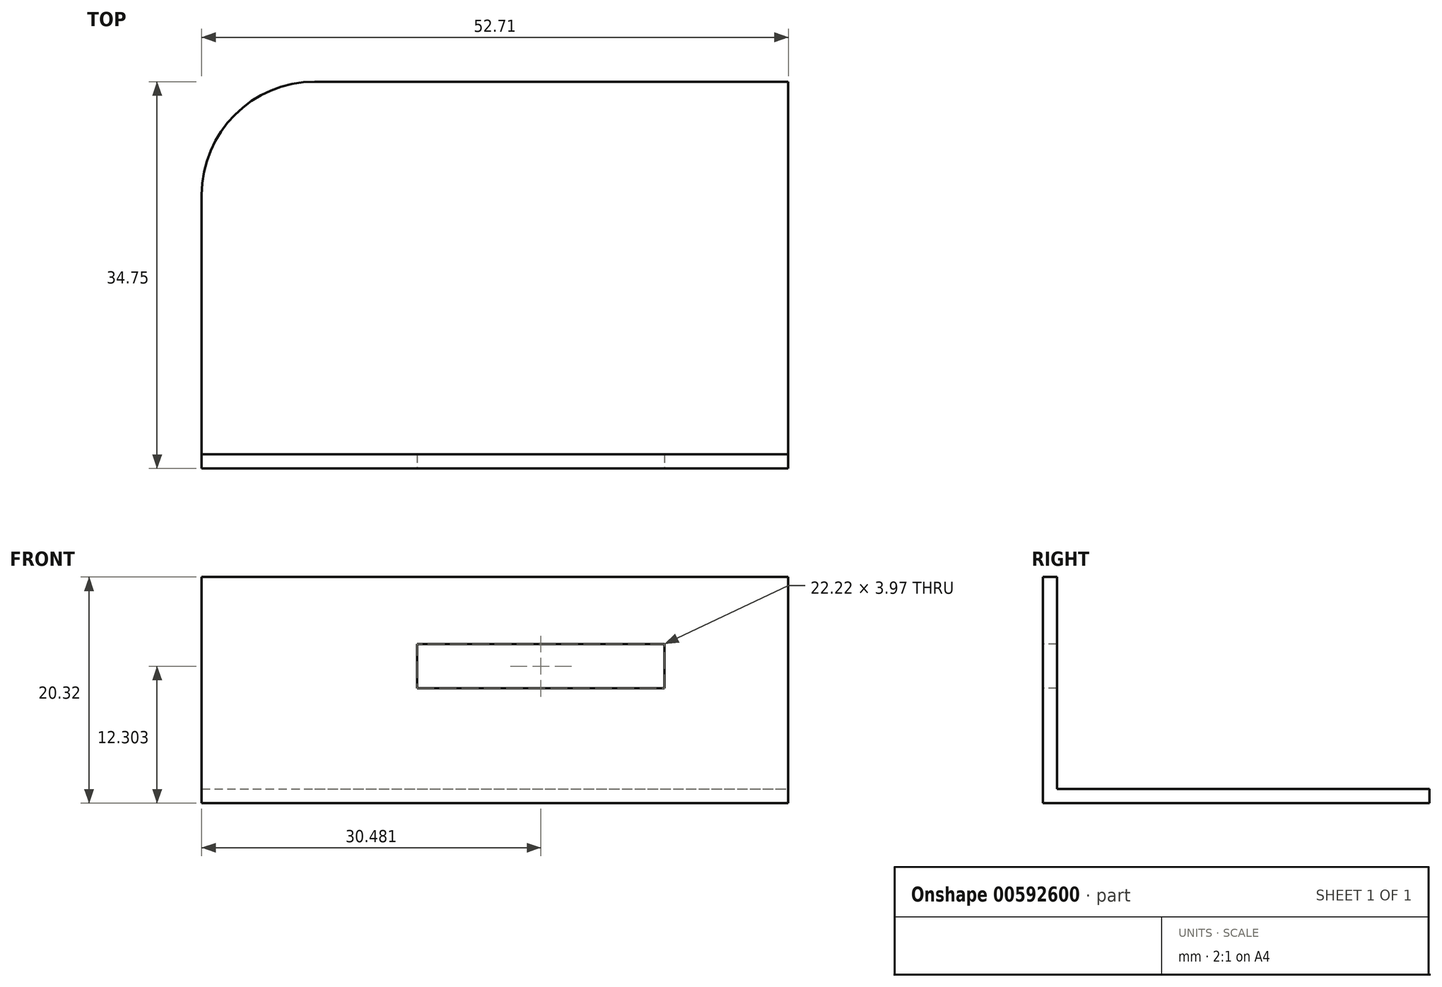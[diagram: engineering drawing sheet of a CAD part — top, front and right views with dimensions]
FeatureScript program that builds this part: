
annotation { "Feature Type Name" : "Feature", "Feature Type Description" : "" }
export const myFeature = defineFeature(function(context is Context, id is Id, definition is map)
    precondition{}
    {
        {
            var Q0;
            Q0=qCreatedBy(makeId("Top.planeOp"),FACE);
            var sketch = newSketch(context, id + "F0", { "sketchPlane" : qUnion([Q0])});
            skLineSegment(sketch, "E0.bottom", {"start": v(-64.95, 19.95) * mm, "end": v(-12.24, 19.95) * mm});
            skLineSegment(sketch, "E0.top", {"start": v(-64.95, -14.8) * mm, "end": v(-12.24, -14.8) * mm});
            skLineSegment(sketch, "E0.left", {"start": v(-64.95, 19.95) * mm, "end": v(-64.95, -14.8) * mm});
            skLineSegment(sketch, "E0.right", {"start": v(-12.24, 19.95) * mm, "end": v(-12.24, -14.8) * mm});
            skLineSegment(sketch, "E1.bottom", {"start": v(-63.68, 18.68) * mm, "end": v(-13.51, 18.68) * mm});
            skLineSegment(sketch, "E1.top", {"start": v(-63.68, -13.53) * mm, "end": v(-13.51, -13.53) * mm});
            skLineSegment(sketch, "E1.left", {"start": v(-63.68, 18.68) * mm, "end": v(-63.68, -13.53) * mm});
            skLineSegment(sketch, "E1.right", {"start": v(-13.51, 18.68) * mm, "end": v(-13.51, -13.53) * mm});
            skSolve(sketch);
        }
        {
            var Q0;
            Q0=makeQuery(id+"F0.imprint","IMPRINT",FACE,{"disambiguationData":[TD([[makeQuery(id+"F0.imprint","IMPRINT",EDGE,{"derivedFrom":sQuery(id+"F0.wireOp",EDGE,"E0.bottom")}),-1.0]])]});
            extrude(context, id + "F1", {"entities" : qUnion([Q0]), "depth" : 20.32 * mm, "offsetDistance" : 25.4 * mm});
        }
        {
            var Q0;
            Q0=makeQuery(id+"F0.imprint","IMPRINT",FACE,{"disambiguationData":[TD([[makeQuery(id+"F0.imprint","IMPRINT",EDGE,{"derivedFrom":sQuery(id+"F0.wireOp",EDGE,"E1.bottom")}),-1.0]])]});
            extrude(context, id + "F2", {"entities" : qUnion([Q0]), "operationType" : NewBodyOperationType.ADD, "depth" : 1.27 * mm, "offsetDistance" : 25.4 * mm});
        }
        {
            var Q0;
            Q0=makeQuery(id+"F1.opExtrude","SWEPT_EDGE",EDGE,{"disambiguationData":[OSD([sQuery(id+"F0.wireOp",EDGE,"E0.bottom"),sQuery(id+"F0.wireOp",EDGE,"E0.left")])]});
            var Q1;
            Q1=makeQuery(id+"F1.opExtrude","SWEPT_EDGE",EDGE,{"disambiguationData":[OSD([sQuery(id+"F0.wireOp",EDGE,"E1.bottom"),sQuery(id+"F0.wireOp",EDGE,"E1.left")])]});
            fillet(context, id + "F3", {"entities" : qUnion([Q0, Q1]), "radius" : 10.16 * mm, "tangentPropagation" : true, "allowEdgeOverflow" : false});
        }
        {
            var Q0;
            Q0=makeQuery(id+"F0.imprint","IMPRINT",FACE,{"disambiguationData":[TD([[makeQuery(id+"F0.imprint","IMPRINT",EDGE,{"derivedFrom":sQuery(id+"F0.wireOp",EDGE,"E0.bottom")}),-1.0]])]});
            var sketch = newSketch(context, id + "F4", { "sketchPlane" : qUnion([Q0])});
            skSolve(sketch);
        }
        {
            var Q0;
            Q0=makeQuery(id+"F1.opExtrude","SWEPT_FACE",FACE,{"disambiguationData":[OSD([sQuery(id+"F0.wireOp",EDGE,"E0.top")])]});
            var sketch = newSketch(context, id + "F5", { "sketchPlane" : qUnion([Q0])});
            skLineSegment(sketch, "E2.bottom", {"start": v(-64.95, 20.32) * mm, "end": v(-12.24, 20.32) * mm});
            skLineSegment(sketch, "E2.top", {"start": v(-64.95, 0) * mm, "end": v(-12.24, 0) * mm});
            skLineSegment(sketch, "E2.left", {"start": v(-64.95, 20.32) * mm, "end": v(-64.95, 0) * mm});
            skLineSegment(sketch, "E2.right", {"start": v(-12.24, 20.32) * mm, "end": v(-12.24, 0) * mm});
            skSolve(sketch);
        }
        {
            var Q0;
            Q0=makeQuery(id+"F1.opExtrude","SWEPT_FACE",FACE,{"disambiguationData":[OSD([sQuery(id+"F0.wireOp",EDGE,"E1.right")])]});
            var sketch = newSketch(context, id + "F6", { "sketchPlane" : qUnion([Q0])});
            skLineSegment(sketch, "E3.bottom", {"start": v(13.53, 10.8) * mm, "end": v(-8.52, 10.8) * mm});
            skLineSegment(sketch, "E3.top", {"start": v(13.53, 9.2) * mm, "end": v(-8.52, 9.2) * mm});
            skLineSegment(sketch, "E3.left", {"start": v(13.53, 10.8) * mm, "end": v(13.53, 9.2) * mm});
            skLineSegment(sketch, "E3.right", {"start": v(-8.52, 10.8) * mm, "end": v(-8.52, 9.2) * mm});
            skLineSegment(sketch, "E4.top", {"start": v(13.53, 7.94) * mm, "end": v(-8.52, 7.94) * mm});
            skLineSegment(sketch, "E4.left", {"start": v(13.53, 9.2) * mm, "end": v(13.53, 7.94) * mm});
            skLineSegment(sketch, "E4.right", {"start": v(-8.52, 9.2) * mm, "end": v(-8.52, 7.94) * mm});
            skSolve(sketch);
        }
        {
            var Q0;
            Q0=makeQuery(id+"F6.imprint","IMPRINT",FACE,{"disambiguationData":[TD([[makeQuery(id+"F6.imprint","IMPRINT",EDGE,{"derivedFrom":sQuery(id+"F6.wireOp",EDGE,"E3.top")}),1.0]])]});
            extrude(context, id + "F7", {"entities" : qUnion([Q0]), "operationType" : NewBodyOperationType.ADD, "depth" : 0.38 * mm, "offsetDistance" : 25.4 * mm});
        }
        {
            var Q0;
            Q0=makeQuery(id+"F1.opExtrude","SWEPT_FACE",FACE,{"disambiguationData":[OSD([sQuery(id+"F0.wireOp",EDGE,"E0.right")])]});
            var sketch = newSketch(context, id + "F8", { "sketchPlane" : qUnion([Q0])});
            skLineSegment(sketch, "E5.bottom", {"start": v(-13.53, 20.32) * mm, "end": v(19.95, 20.32) * mm});
            skLineSegment(sketch, "E5.top", {"start": v(-13.53, 1.27) * mm, "end": v(19.95, 1.27) * mm});
            skLineSegment(sketch, "E5.left", {"start": v(-13.53, 20.32) * mm, "end": v(-13.53, 1.27) * mm});
            skLineSegment(sketch, "E5.right", {"start": v(19.95, 20.32) * mm, "end": v(19.95, 1.27) * mm});
            skSolve(sketch);
        }
        {
            var Q0;
            Q0 = qSketchRegion(id + "F8", true);
            extrude(context, id + "F9", {"entities" : qUnion([Q0]), "operationType" : NewBodyOperationType.REMOVE, "oppositeDirection" : true, "depth" : 78.74 * mm, "offsetDistance" : 25.4 * mm});
        }
        {
            var Q0;
            Q0=makeQuery(id+"F5.imprint","IMPRINT",FACE,{"disambiguationData":[TD([[makeQuery(id+"F5.imprint","IMPRINT",EDGE,{"derivedFrom":sQuery(id+"F5.wireOp",EDGE,"E2.bottom")}),-1.0]])]});
            var sketch = newSketch(context, id + "F10", { "sketchPlane" : qUnion([Q0])});
            skLineSegment(sketch, "E6.bottom", {"start": v(-45.58, 14.29) * mm, "end": v(-23.36, 14.29) * mm});
            skLineSegment(sketch, "E6.top", {"start": v(-45.58, 10.32) * mm, "end": v(-23.36, 10.32) * mm});
            skLineSegment(sketch, "E6.left", {"start": v(-45.58, 14.29) * mm, "end": v(-45.58, 10.32) * mm});
            skLineSegment(sketch, "E6.right", {"start": v(-23.36, 14.29) * mm, "end": v(-23.36, 10.32) * mm});
            skSolve(sketch);
        }
        {
            var Q0;
            Q0 = qSketchRegion(id + "F10", true);
            extrude(context, id + "F11", {"entities" : qUnion([Q0]), "operationType" : NewBodyOperationType.REMOVE, "oppositeDirection" : true, "depth" : 25.4 * mm, "offsetDistance" : 25.4 * mm});
        }
    });
